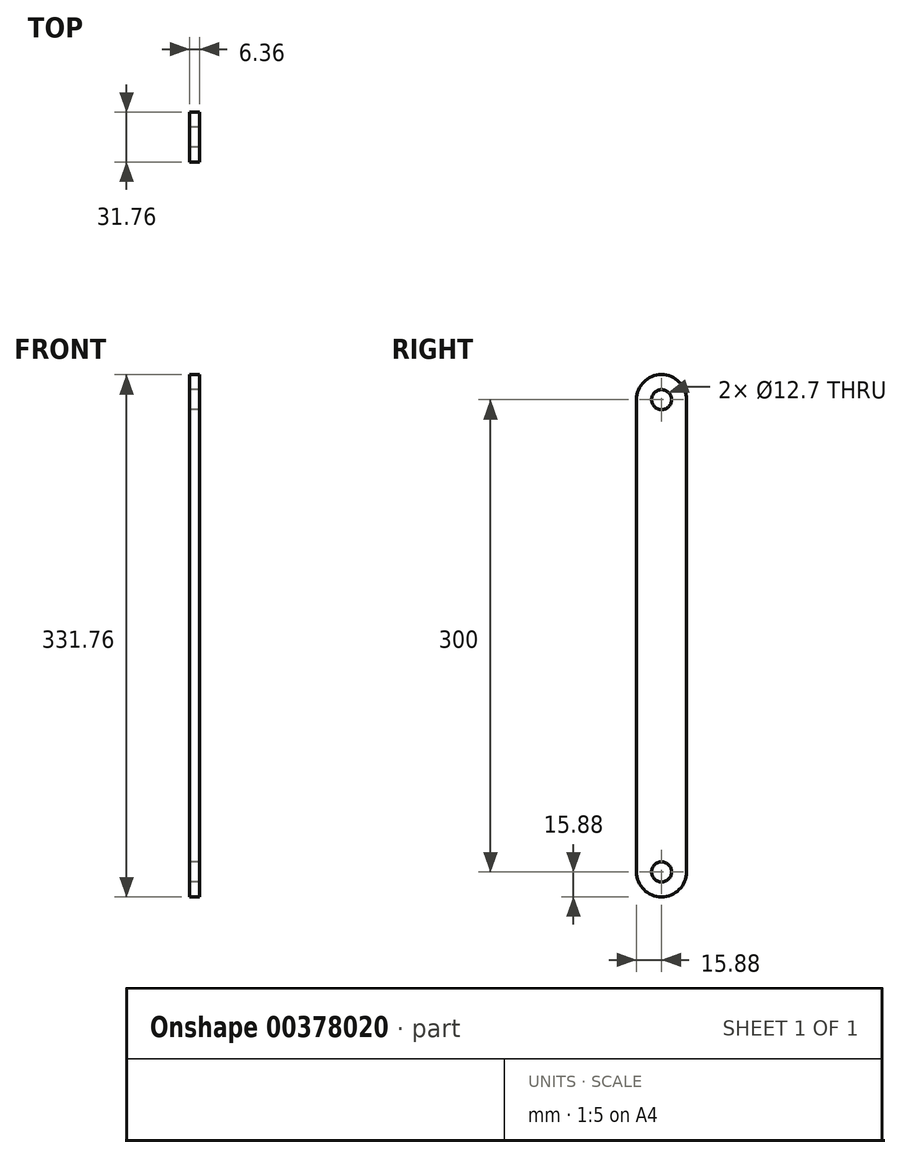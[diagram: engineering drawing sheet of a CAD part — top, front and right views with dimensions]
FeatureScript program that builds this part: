
annotation { "Feature Type Name" : "Feature", "Feature Type Description" : "" }
export const myFeature = defineFeature(function(context is Context, id is Id, definition is map)
    precondition{}
    {
        {
            var Q0;
            Q0=qCreatedBy(makeId("Right.planeOp"),FACE);
            var sketch = newSketch(context, id + "F0", { "sketchPlane" : qUnion([Q0])});
            skCircle(sketch, "E0", {"center": v(0, 0) * mm, "radius": 6.35 * mm});
            skArc(sketch, "E1", {"start": v(15.88, 0) * mm, "mid": v(0, 15.88) * mm, "end": v(-15.88, 0) * mm});
            skCircle(sketch, "E2", {"center": v(0, -300) * mm, "radius": 6.35 * mm});
            skArc(sketch, "E3", {"start": v(-15.88, -300) * mm, "mid": v(0, -315.88) * mm, "end": v(15.88, -300) * mm});
            skLineSegment(sketch, "E4", {"start": v(-15.88, 0) * mm, "end": v(-15.88, -300) * mm});
            skLineSegment(sketch, "E5", {"start": v(15.88, 0) * mm, "end": v(15.88, -300) * mm});
            skSolve(sketch);
        }
        {
            var Q0;
            Q0 = qSketchRegion(id + "F0", true);
            extrude(context, id + "F1", {"entities" : qUnion([Q0]), "endBound" : BoundingType.SYMMETRIC, "depth" : 6.35 * mm});
        }
    });
